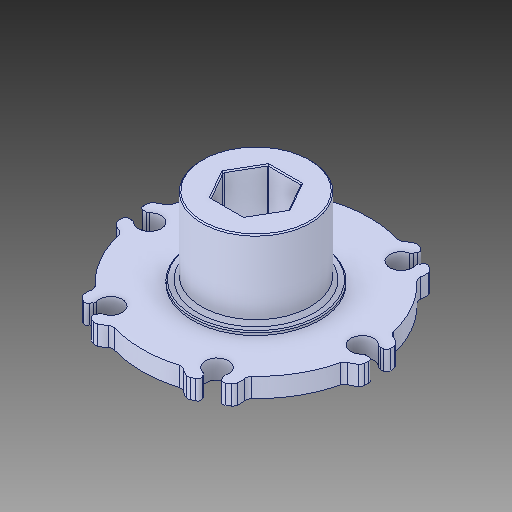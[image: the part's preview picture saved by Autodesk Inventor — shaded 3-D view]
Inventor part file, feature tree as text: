
AUTODESK INVENTOR PART (.ipt)
format: ipt  version: 2018.2 (Build 222227000, 227)  size: 285,696 bytes
history: native  units: in
note: dims shown in document units (in); Inventor stores cm internally (conversion verified against a paired STEP export)
features: fillet x1
ambient origin geometry x8: Origin, YZ Plane, XZ Plane, XY Plane, X Axis, Y Axis, Z Axis, Center Point
bodies: Solid1 (feature_tree)
feature tree (1):
  fillet  "Fillet7"  [1 undecoded]
note: 1 required parameter value undecoded (feature->parameter linkage not recoverable at this tier; creation-order binding heuristic only, values carry confidence <= 0.55)
